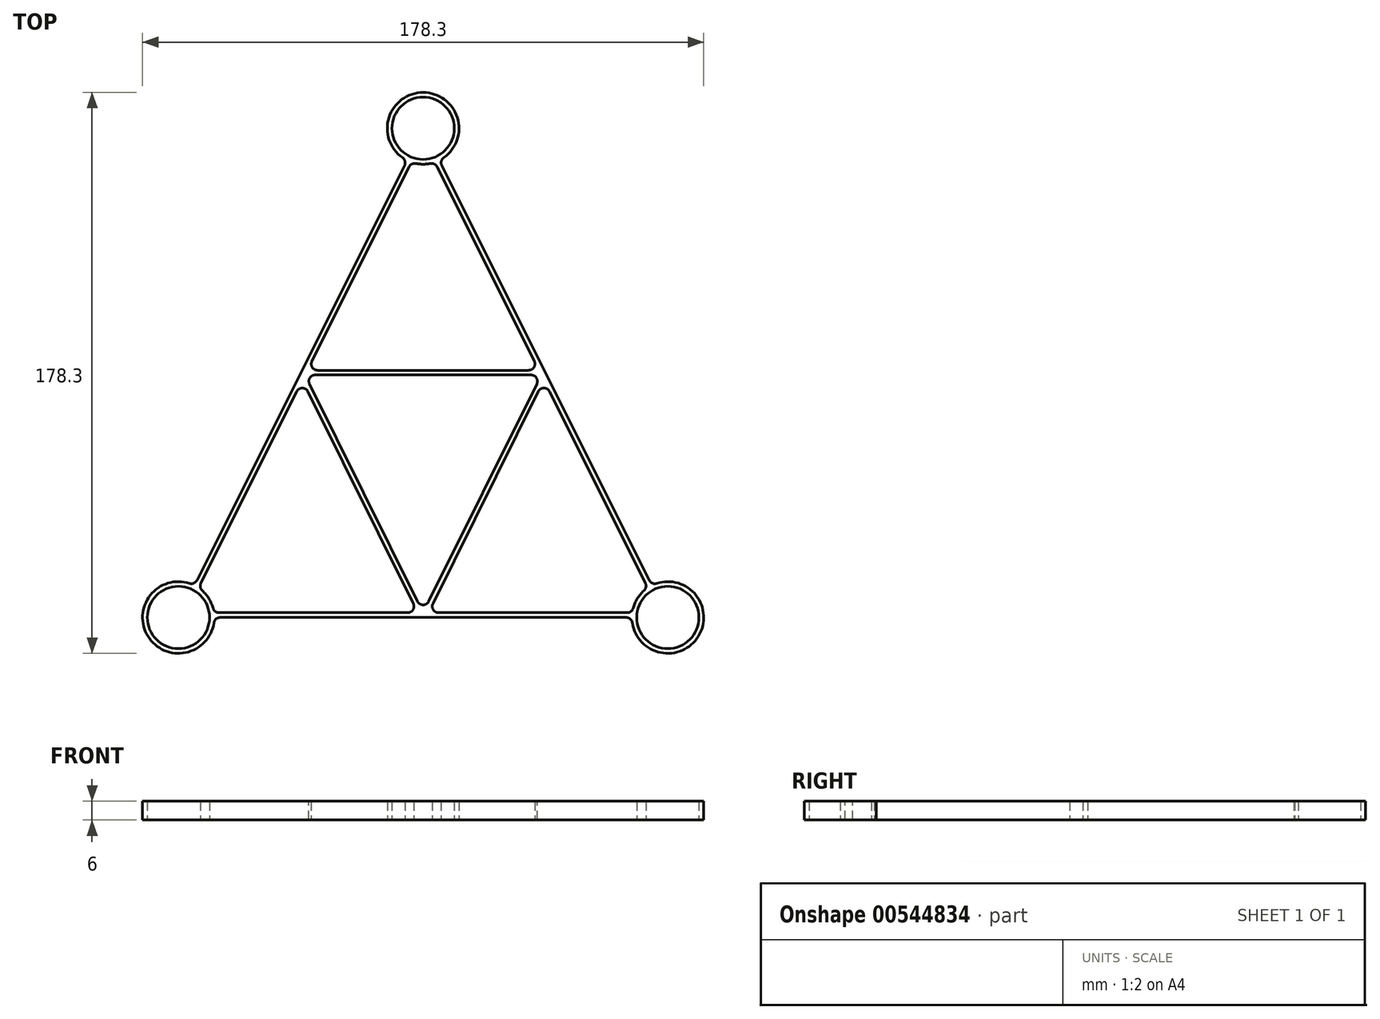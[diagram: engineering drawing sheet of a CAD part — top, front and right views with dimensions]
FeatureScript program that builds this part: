
annotation { "Feature Type Name" : "Feature", "Feature Type Description" : "" }
export const myFeature = defineFeature(function(context is Context, id is Id, definition is map)
    precondition{}
    {
        {
            var Q0;
            Q0=qCreatedBy(makeId("Top.planeOp"),FACE);
            var sketch = newSketch(context, id + "F0", { "sketchPlane" : qUnion([Q0])});
            skLineSegment(sketch, "E0.bottom", {"start": v(89, 89) * mm, "end": v(-89, 89) * mm, "construction": true});
            skLineSegment(sketch, "E0.top", {"start": v(89, -89) * mm, "end": v(-89, -89) * mm, "construction": true});
            skLineSegment(sketch, "E0.left", {"start": v(89, 89) * mm, "end": v(89, -89) * mm, "construction": true});
            skLineSegment(sketch, "E0.right", {"start": v(-89, 89) * mm, "end": v(-89, -89) * mm, "construction": true});
            skPoint(sketch, "E0.middle", {"position": v(0, 0) * mm});
            skLineSegment(sketch, "E1.0", {"start": v(77.75, 77.75) * mm, "end": v(-77.75, 77.75) * mm, "construction": true});
            skLineSegment(sketch, "E1.1", {"start": v(77.75, 77.75) * mm, "end": v(77.75, -77.75) * mm, "construction": true});
            skLineSegment(sketch, "E1.2", {"start": v(66.35, -77.75) * mm, "end": v(-66.35, -77.75) * mm});
            skLineSegment(sketch, "E1.3", {"start": v(-77.75, 77.75) * mm, "end": v(-77.75, -77.75) * mm, "construction": true});
            skCircle(sketch, "E2", {"center": v(0, 77.75) * mm, "radius": 9.9 * mm});
            skCircle(sketch, "E3", {"center": v(-77.75, -77.75) * mm, "radius": 9.9 * mm});
            skCircle(sketch, "E4", {"center": v(77.75, -77.75) * mm, "radius": 9.9 * mm});
            skLineSegment(sketch, "E5", {"start": v(-72.65, -67.55) * mm, "end": v(-5.1, 67.55) * mm});
            skLineSegment(sketch, "E6", {"start": v(5.1, 67.55) * mm, "end": v(72.65, -67.55) * mm});
            skArc(sketch, "E7.0", {"start": v(-66.45, -76.25) * mm, "mid": v(-68.05, -71.76) * mm, "end": v(-71.35, -68.31) * mm});
            skArc(sketch, "E8.0", {"start": v(5.1, 67.55) * mm, "mid": v(0, 89.15) * mm, "end": v(-5.1, 67.55) * mm});
            skArc(sketch, "E9.0", {"start": v(71.35, -68.31) * mm, "mid": v(68.05, -71.76) * mm, "end": v(66.45, -76.25) * mm});
            skLineSegment(sketch, "E10.0", {"start": v(-71.35, -68.31) * mm, "end": v(-38.37, -2.35) * mm});
            skLineSegment(sketch, "E10.1", {"start": v(66.45, -76.25) * mm, "end": v(1.67, -76.25) * mm});
            skLineSegment(sketch, "E10.2", {"start": v(3.71, 66.97) * mm, "end": v(36.78, 0.83) * mm});
            skArc(sketch, "E11.trimOffspring", {"start": v(-3.71, 66.97) * mm, "mid": v(0, 66.35) * mm, "end": v(3.71, 66.97) * mm});
            skArc(sketch, "E12.trimOffspring", {"start": v(-72.65, -67.55) * mm, "mid": v(-87.45, -83.74) * mm, "end": v(-66.35, -77.75) * mm});
            skArc(sketch, "E13.trimOffspring", {"start": v(66.35, -77.75) * mm, "mid": v(87.45, -83.74) * mm, "end": v(72.65, -67.55) * mm});
            skLineSegment(sketch, "E14", {"start": v(0, -76.25) * mm, "end": v(-37.53, -0.67) * mm});
            skLineSegment(sketch, "E15", {"start": v(-37.53, -0.67) * mm, "end": v(37.53, -0.67) * mm});
            skLineSegment(sketch, "E16", {"start": v(37.53, -0.67) * mm, "end": v(0, -76.25) * mm});
            skLineSegment(sketch, "E17.0", {"start": v(-36.78, 0.83) * mm, "end": v(36.78, 0.83) * mm});
            skLineSegment(sketch, "E17.1", {"start": v(-1.67, -76.25) * mm, "end": v(-38.37, -2.35) * mm});
            skLineSegment(sketch, "E17.2", {"start": v(38.37, -2.35) * mm, "end": v(1.67, -76.25) * mm});
            skLineSegment(sketch, "E18.trimOffspring", {"start": v(-1.67, -76.25) * mm, "end": v(-66.45, -76.25) * mm});
            skLineSegment(sketch, "E19.trimOffspring", {"start": v(-36.78, 0.83) * mm, "end": v(-3.71, 66.97) * mm});
            skLineSegment(sketch, "E20.trimOffspring", {"start": v(38.37, -2.35) * mm, "end": v(71.35, -68.31) * mm});
            skSolve(sketch);
        }
        {
            var Q0;
            Q0=makeQuery(id+"F0.imprint","IMPRINT",FACE,{"disambiguationData":[TD([[makeQuery(id+"F0.imprint","IMPRINT",EDGE,{"derivedFrom":sQuery(id+"F0.wireOp",EDGE,"E1.2")}),-1.0]])]});
            extrude(context, id + "F1", {"entities" : qUnion([Q0]), "depth" : 6 * mm, "offsetDistance" : 25 * mm});
        }
        {
            var Q0;
            Q0=makeQuery(id+"F1.opExtrude","SWEPT_EDGE",EDGE,{"disambiguationData":[OSD([sQuery(id+"F0.wireOp",EDGE,"E14"),sQuery(id+"F0.wireOp",EDGE,"E15")])]});
            var Q1;
            Q1=makeQuery(id+"F1.opExtrude","SWEPT_EDGE",EDGE,{"disambiguationData":[OSD([sQuery(id+"F0.wireOp",EDGE,"E11.trimOffspring"),sQuery(id+"F0.wireOp",EDGE,"E19.trimOffspring")])]});
            var Q2;
            Q2=makeQuery(id+"F1.opExtrude","SWEPT_EDGE",EDGE,{"disambiguationData":[OSD([sQuery(id+"F0.wireOp",EDGE,"E6"),sQuery(id+"F0.wireOp",EDGE,"E8.0")])]});
            var Q3;
            Q3=makeQuery(id+"F1.opExtrude","SWEPT_EDGE",EDGE,{"disambiguationData":[OSD([sQuery(id+"F0.wireOp",EDGE,"E10.2"),sQuery(id+"F0.wireOp",EDGE,"E11.trimOffspring")])]});
            var Q4;
            Q4=makeQuery(id+"F1.opExtrude","SWEPT_EDGE",EDGE,{"disambiguationData":[OSD([sQuery(id+"F0.wireOp",EDGE,"E5"),sQuery(id+"F0.wireOp",EDGE,"E8.0")])]});
            var Q5;
            Q5=makeQuery(id+"F1.opExtrude","SWEPT_EDGE",EDGE,{"disambiguationData":[OSD([sQuery(id+"F0.wireOp",EDGE,"E17.2"),sQuery(id+"F0.wireOp",EDGE,"E20.trimOffspring")])]});
            var Q6;
            Q6=makeQuery(id+"F1.opExtrude","SWEPT_EDGE",EDGE,{"disambiguationData":[OSD([sQuery(id+"F0.wireOp",EDGE,"E15"),sQuery(id+"F0.wireOp",EDGE,"E16")])]});
            var Q7;
            Q7=makeQuery(id+"F1.opExtrude","SWEPT_EDGE",EDGE,{"disambiguationData":[OSD([sQuery(id+"F0.wireOp",EDGE,"E10.2"),sQuery(id+"F0.wireOp",EDGE,"E17.0")])]});
            var Q8;
            Q8=makeQuery(id+"F1.opExtrude","SWEPT_EDGE",EDGE,{"disambiguationData":[OSD([sQuery(id+"F0.wireOp",EDGE,"E10.1"),sQuery(id+"F0.wireOp",EDGE,"E17.2")])]});
            var Q9;
            Q9=makeQuery(id+"F1.opExtrude","SWEPT_EDGE",EDGE,{"disambiguationData":[OSD([sQuery(id+"F0.wireOp",EDGE,"E14"),sQuery(id+"F0.wireOp",EDGE,"E16")])]});
            var Q10;
            Q10=makeQuery(id+"F1.opExtrude","SWEPT_EDGE",EDGE,{"disambiguationData":[OSD([sQuery(id+"F0.wireOp",EDGE,"E17.1"),sQuery(id+"F0.wireOp",EDGE,"E18.trimOffspring")])]});
            var Q11;
            Q11=makeQuery(id+"F1.opExtrude","SWEPT_EDGE",EDGE,{"disambiguationData":[OSD([sQuery(id+"F0.wireOp",EDGE,"E9.0"),sQuery(id+"F0.wireOp",EDGE,"E20.trimOffspring")])]});
            var Q12;
            Q12=makeQuery(id+"F1.opExtrude","SWEPT_EDGE",EDGE,{"disambiguationData":[OSD([sQuery(id+"F0.wireOp",EDGE,"E9.0"),sQuery(id+"F0.wireOp",EDGE,"E10.1")])]});
            var Q13;
            Q13=makeQuery(id+"F1.opExtrude","SWEPT_EDGE",EDGE,{"disambiguationData":[OSD([sQuery(id+"F0.wireOp",EDGE,"E1.2"),sQuery(id+"F0.wireOp",EDGE,"E13.trimOffspring")])]});
            var Q14;
            Q14=makeQuery(id+"F1.opExtrude","SWEPT_EDGE",EDGE,{"disambiguationData":[OSD([sQuery(id+"F0.wireOp",EDGE,"E6"),sQuery(id+"F0.wireOp",EDGE,"E13.trimOffspring")])]});
            var Q15;
            Q15=makeQuery(id+"F1.opExtrude","SWEPT_EDGE",EDGE,{"disambiguationData":[OSD([sQuery(id+"F0.wireOp",EDGE,"E1.2"),sQuery(id+"F0.wireOp",EDGE,"E12.trimOffspring")])]});
            var Q16;
            Q16=makeQuery(id+"F1.opExtrude","SWEPT_EDGE",EDGE,{"disambiguationData":[OSD([sQuery(id+"F0.wireOp",EDGE,"E5"),sQuery(id+"F0.wireOp",EDGE,"E12.trimOffspring")])]});
            var Q17;
            Q17=makeQuery(id+"F1.opExtrude","SWEPT_EDGE",EDGE,{"disambiguationData":[OSD([sQuery(id+"F0.wireOp",EDGE,"E7.0"),sQuery(id+"F0.wireOp",EDGE,"E18.trimOffspring")])]});
            var Q18;
            Q18=makeQuery(id+"F1.opExtrude","SWEPT_EDGE",EDGE,{"disambiguationData":[OSD([sQuery(id+"F0.wireOp",EDGE,"E7.0"),sQuery(id+"F0.wireOp",EDGE,"E10.0")])]});
            var Q19;
            Q19=makeQuery(id+"F1.opExtrude","SWEPT_EDGE",EDGE,{"disambiguationData":[OSD([sQuery(id+"F0.wireOp",EDGE,"E17.0"),sQuery(id+"F0.wireOp",EDGE,"E19.trimOffspring")])]});
            var Q20;
            Q20=makeQuery(id+"F1.opExtrude","SWEPT_EDGE",EDGE,{"disambiguationData":[OSD([sQuery(id+"F0.wireOp",EDGE,"E10.0"),sQuery(id+"F0.wireOp",EDGE,"E17.1")])]});
            fillet(context, id + "F2", {"entities" : qUnion([Q0, Q1, Q2, Q3, Q4, Q5, Q6, Q7, Q8, Q9, Q10, Q11, Q12, Q13, Q14, Q15, Q16, Q17, Q18, Q19, Q20]), "radius" : 2 * mm, "tangentPropagation" : true, "allowEdgeOverflow" : false});
        }
    });
